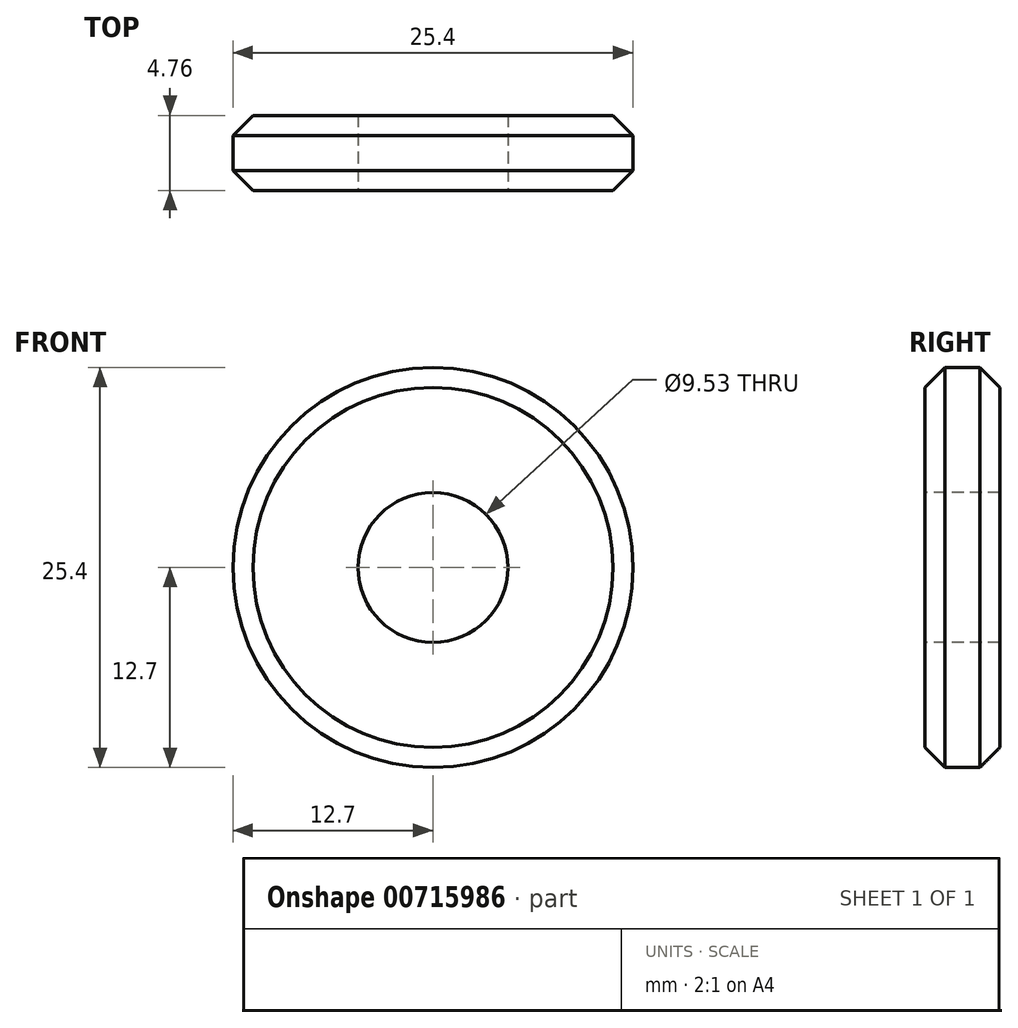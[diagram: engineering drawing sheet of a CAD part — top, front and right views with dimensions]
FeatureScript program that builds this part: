
annotation { "Feature Type Name" : "Feature", "Feature Type Description" : "" }
export const myFeature = defineFeature(function(context is Context, id is Id, definition is map)
    precondition{}
    {
        {
            var Q0;
            Q0=qCreatedBy(makeId("Front.planeOp"),FACE);
            var sketch = newSketch(context, id + "F0", { "sketchPlane" : qUnion([Q0])});
            skCircle(sketch, "E0", {"center": v(0, 0) * mm, "radius": 4.76 * mm});
            skCircle(sketch, "E1", {"center": v(0, 0) * mm, "radius": 12.7 * mm});
            skSolve(sketch);
        }
        {
            var Q0;
            Q0=makeQuery(id+"F0.imprint","IMPRINT",FACE,{"disambiguationData":[TD([[makeQuery(id+"F0.imprint","IMPRINT",EDGE,{"derivedFrom":sQuery(id+"F0.wireOp",EDGE,"E0")}),-1.0]])]});
            extrude(context, id + "F1", {"entities" : qUnion([Q0]), "oppositeDirection" : true, "depth" : 4.76 * mm, "offsetDistance" : 25.4 * mm});
        }
        {
            var Q0;
            Q0=makeQuery(id+"F1.opExtrude","CAP_EDGE",EDGE,{"disambiguationData":[OSD([sQuery(id+"F0.wireOp",EDGE,"E1")])],"isStart":true});
            var Q1;
            Q1=makeQuery(id+"F1.opExtrude","CAP_EDGE",EDGE,{"disambiguationData":[OSD([sQuery(id+"F0.wireOp",EDGE,"E1")])],"isStart":false});
            chamfer(context, id + "F2", {"entities" : qUnion([Q0, Q1]), "width" : 1.27 * mm, "tangentPropagation" : true});
        }
    });
